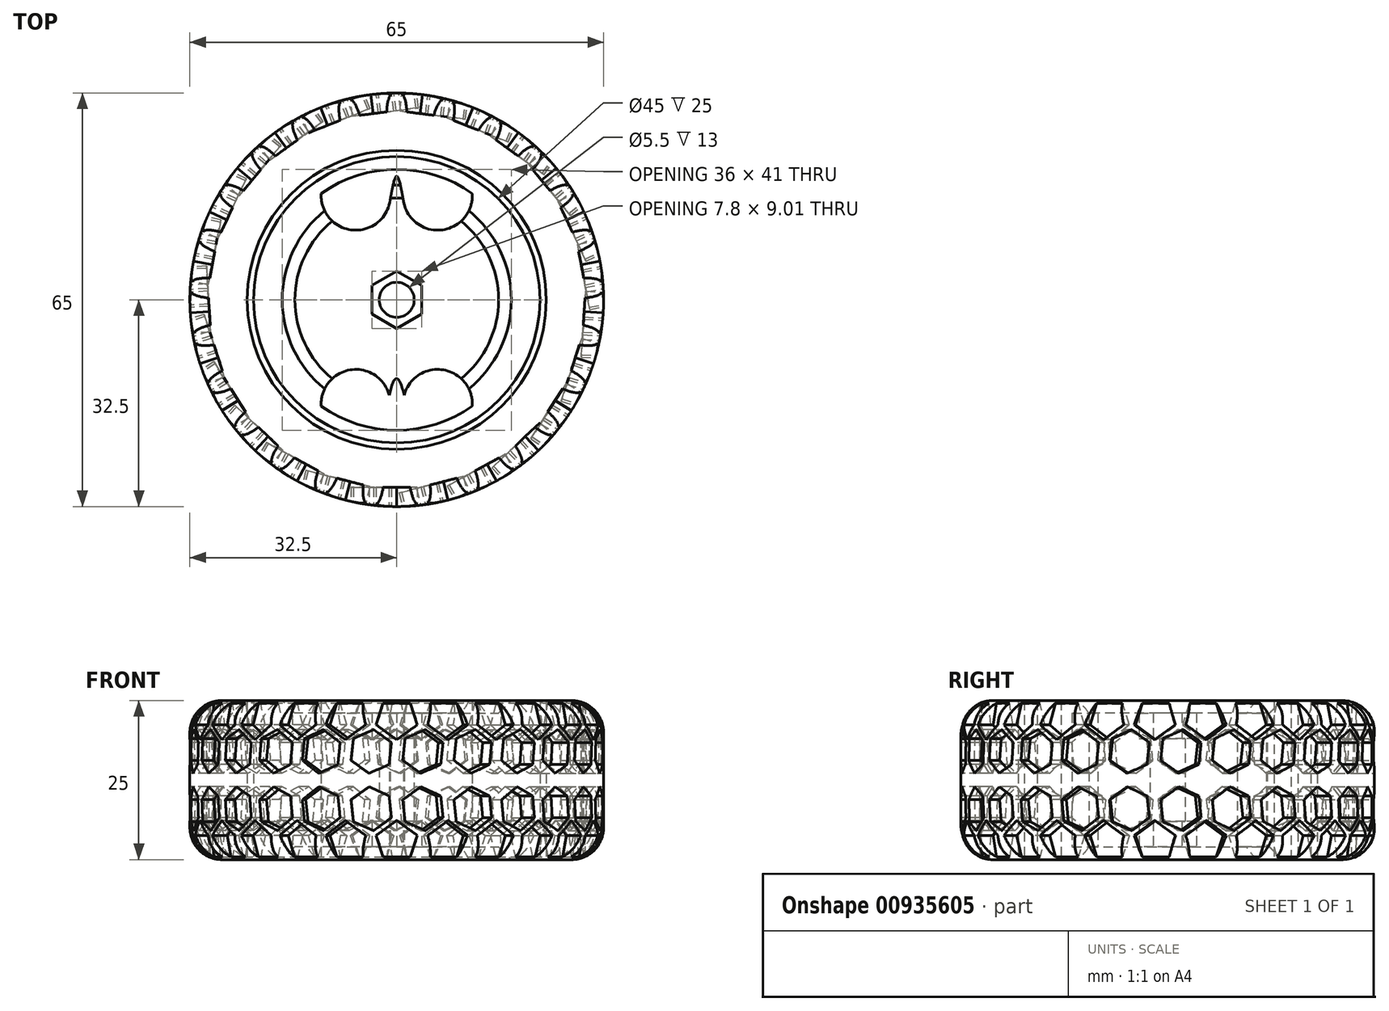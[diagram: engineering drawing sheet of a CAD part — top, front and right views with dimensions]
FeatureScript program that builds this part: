
annotation { "Feature Type Name" : "Feature", "Feature Type Description" : "" }
export const myFeature = defineFeature(function(context is Context, id is Id, definition is map)
    precondition{}
    {
        {
            var Q0;
            Q0=qCreatedBy(makeId("Top.planeOp"),FACE);
            var sketch = newSketch(context, id + "F0", { "sketchPlane" : qUnion([Q0])});
            skCircle(sketch, "E0", {"center": v(0, 0) * mm, "radius": 32.5 * mm});
            skCircle(sketch, "E1", {"center": v(0, 0) * mm, "radius": 22.5 * mm});
            skCircle(sketch, "E2", {"center": v(0, 0) * mm, "radius": 23.5 * mm});
            skCircle(sketch, "E3", {"center": v(0, 0) * mm, "radius": 20.5 * mm});
            skCircle(sketch, "E4", {"center": v(0, 0) * mm, "radius": 6 * mm});
            skCircle(sketch, "E5.cCircle", {"center": v(0, 0) * mm, "radius": 3.9 * mm, "construction": true});
            skLineSegment(sketch, "E5.0", {"start": v(-3.9, -2.25) * mm, "end": v(-3.9, 2.25) * mm});
            skLineSegment(sketch, "E5.1", {"start": v(-3.9, 2.25) * mm, "end": v(0, 4.5) * mm});
            skLineSegment(sketch, "E5.2", {"start": v(0, 4.5) * mm, "end": v(3.9, 2.25) * mm});
            skLineSegment(sketch, "E5.3", {"start": v(3.9, 2.25) * mm, "end": v(3.9, -2.25) * mm});
            skLineSegment(sketch, "E5.4", {"start": v(3.9, -2.25) * mm, "end": v(0, -4.5) * mm});
            skLineSegment(sketch, "E5.5", {"start": v(0, -4.5) * mm, "end": v(-3.9, -2.25) * mm});
            skPoint(sketch, "E5.0.midPoint", {"position": v(-3.9, 0) * mm});
            skCircle(sketch, "E6", {"center": v(0, 0) * mm, "radius": 3 * mm});
            skCircle(sketch, "E7", {"center": v(0, 0) * mm, "radius": 2.75 * mm});
            skArc(sketch, "E8", {"start": v(2.68, 20.32) * mm, "mid": v(4.44, 11.32) * mm, "end": v(11.87, 16.72) * mm});
            skArc(sketch, "E9.MirrorCS", {"start": v(-2.68, 20.32) * mm, "mid": v(-4.44, 11.32) * mm, "end": v(-11.87, 16.72) * mm});
            skArc(sketch, "E10.MirrorCS", {"start": v(-2.68, -20.32) * mm, "mid": v(-4.44, -11.32) * mm, "end": v(-11.87, -16.72) * mm});
            skArc(sketch, "E11.MirrorCS", {"start": v(2.68, -20.32) * mm, "mid": v(4.44, -11.32) * mm, "end": v(11.87, -16.72) * mm});
            skFitSpline(sketch, "E12", {"points": [v(-1.04, 15.65) * mm, v(0, 19.44) * mm, v(1.06, 15.51) * mm], "startDerivative": vector(2.1, 11.48) * mm, "endDerivative": vector(2.1, -11.69) * mm});
            skFitSpline(sketch, "E13", {"points": [v(-1.17, -15) * mm, v(1.17, -15) * mm], "startDerivative": vector(2.28, 10.68) * mm, "endDerivative": vector(2.46, -10.47) * mm});
            skSolve(sketch);
        }
        {
            var Q0;
            {var subQ0=sQuery(id+"F0.wireOp",EDGE,"820db2d4-8ff4-4f6f-a6e0-25a010e94ee20.MirrorCS");var subQ1=sQuery(id+"F0.wireOp",EDGE,"E3");var subQ2=makeQuery(id+"F0.imprint","INTERSECT",VERTEX,{"disambiguationData":[OD(0.0)],"derivedFrom":[subQ1,subQ0]});Q0=makeQuery(id+"F0.imprint","IMPRINT",FACE,{"disambiguationData":[TD([[makeQuery(id+"F0.imprint","IMPRINT",EDGE,{"disambiguationData":[TD([[subQ2,1.0]])],"derivedFrom":subQ1}),1.0]])]});}
            var Q1;
            Q1=makeQuery(id+"F0.imprint","IMPRINT",FACE,{"disambiguationData":[TD([[makeQuery(id+"F0.imprint","IMPRINT",EDGE,{"derivedFrom":sQuery(id+"F0.wireOp",EDGE,"E1")}),1.0]])]});
            var Q2;
            {var subQ0=sQuery(id+"F0.wireOp",EDGE,"fe73a623-ffbc-4a68-a9c5-13096b3fdf640.MirrorCS");var subQ1=sQuery(id+"F0.wireOp",EDGE,"E3");var subQ2=makeQuery(id+"F0.imprint","INTERSECT",VERTEX,{"disambiguationData":[OD(1.0)],"derivedFrom":[subQ1,subQ0]});Q2=makeQuery(id+"F0.imprint","IMPRINT",FACE,{"disambiguationData":[TD([[makeQuery(id+"F0.imprint","IMPRINT",EDGE,{"disambiguationData":[TD([[subQ2,1.0]])],"derivedFrom":subQ1}),1.0]])]});}
            var Q3;
            {var subQ0=sQuery(id+"F0.wireOp",EDGE,"6e8611d1-8290-4c50-aa15-6a44690360f50.MirrorCS");var subQ1=sQuery(id+"F0.wireOp",EDGE,"E3");var subQ2=makeQuery(id+"F0.imprint","INTERSECT",VERTEX,{"disambiguationData":[OD(1.0)],"derivedFrom":[subQ1,subQ0]});Q3=makeQuery(id+"F0.imprint","IMPRINT",FACE,{"disambiguationData":[TD([[makeQuery(id+"F0.imprint","IMPRINT",EDGE,{"disambiguationData":[TD([[subQ2,-1.0]])],"derivedFrom":subQ1}),1.0]])]});}
            var Q4;
            {var subQ0=sQuery(id+"F0.wireOp",EDGE,"6e8611d1-8290-4c50-aa15-6a44690360f50.MirrorCS");var subQ1=sQuery(id+"F0.wireOp",EDGE,"E3");var subQ2=makeQuery(id+"F0.imprint","INTERSECT",VERTEX,{"disambiguationData":[OD(0.0)],"derivedFrom":[subQ1,subQ0]});Q4=makeQuery(id+"F0.imprint","IMPRINT",FACE,{"disambiguationData":[TD([[makeQuery(id+"F0.imprint","IMPRINT",EDGE,{"disambiguationData":[TD([[subQ2,1.0]])],"derivedFrom":subQ1}),1.0]])]});}
            var Q5;
            Q5=makeQuery(id+"F0.imprint","IMPRINT",FACE,{"disambiguationData":[TD([[makeQuery(id+"F0.imprint","IMPRINT",EDGE,{"derivedFrom":sQuery(id+"F0.wireOp",EDGE,"E5.0")}),1.0]])]});
            var Q6;
            Q6=makeQuery(id+"F0.imprint","IMPRINT",FACE,{"disambiguationData":[TD([[makeQuery(id+"F0.imprint","IMPRINT",EDGE,{"derivedFrom":sQuery(id+"F0.wireOp",EDGE,"E5.0")}),-1.0]])]});
            var Q7;
            Q7=makeQuery(id+"F0.imprint","IMPRINT",FACE,{"disambiguationData":[TD([[makeQuery(id+"F0.imprint","IMPRINT",EDGE,{"derivedFrom":sQuery(id+"F0.wireOp",EDGE,"E1")}),-1.0]])]});
            var Q8;
            Q8=makeQuery(id+"F0.imprint","IMPRINT",FACE,{"disambiguationData":[TD([[makeQuery(id+"F0.imprint","IMPRINT",EDGE,{"derivedFrom":sQuery(id+"F0.wireOp",EDGE,"E4")}),-1.0]])]});
            extrude(context, id + "F1", {"entities" : qUnion([Q0, Q1, Q2, Q3, Q4, Q5, Q6, Q7, Q8]), "depth" : 25 * mm, "offsetDistance" : 25 * mm});
        }
        {
            var Q0;
            Q0=makeQuery(id+"F0.imprint","IMPRINT",FACE,{"disambiguationData":[TD([[makeQuery(id+"F0.imprint","IMPRINT",EDGE,{"derivedFrom":sQuery(id+"F0.wireOp",EDGE,"E0")}),1.0]])]});
            var Q1;
            Q1=makeQuery(id+"F0.imprint","IMPRINT",FACE,{"disambiguationData":[TD([[makeQuery(id+"F0.imprint","IMPRINT",EDGE,{"derivedFrom":sQuery(id+"F0.wireOp",EDGE,"E1")}),-1.0]])]});
            extrude(context, id + "F2", {"entities" : qUnion([Q0, Q1]), "depth" : 25 * mm, "offsetDistance" : 25 * mm});
        }
        {
            var Q0;
            Q0=makeQuery(id+"F0.imprint","IMPRINT",FACE,{"disambiguationData":[TD([[makeQuery(id+"F0.imprint","IMPRINT",EDGE,{"derivedFrom":sQuery(id+"F0.wireOp",EDGE,"E6")}),1.0]])]});
            extrude(context, id + "F3", {"entities" : qUnion([Q0]), "operationType" : NewBodyOperationType.ADD, "depth" : 23 * mm, "offsetDistance" : 25 * mm, "hasSecondDirection" : true, "secondDirectionOppositeDirection" : false, "secondDirectionDepth" : 2 * mm});
        }
        {
            var Q0;
            Q0=makeQuery(id+"F1.opExtrude","CAP_EDGE",EDGE,{"disambiguationData":[OSD([sQuery(id+"F0.wireOp",EDGE,"E6")])],"isStart":true});
            var Q1;
            Q1=makeQuery(id+"F1.opExtrude","CAP_EDGE",EDGE,{"disambiguationData":[OSD([sQuery(id+"F0.wireOp",EDGE,"E6")])],"isStart":false});
            chamfer(context, id + "F4", {"entities" : qUnion([Q0, Q1]), "width" : 15 * mm, "tangentPropagation" : true});
        }
        {
            var Q0;
            Q0=qCreatedBy(makeId("Front.planeOp"),FACE);
            cPlane(context, id + "F5", {"entities" : qUnion([Q0]), "cplaneType" : CPlaneType.OFFSET, "offset" : 32.5 * mm, "width" : 150 * mm, "height" : 150 * mm});
        }
        {
            var Q0;
            Q0=qCreatedBy(id+"F5.planeOp",FACE);
            var sketch = newSketch(context, id + "F6", { "sketchPlane" : qUnion([Q0])});
            skCircle(sketch, "E14.cCircle", {"center": v(0, 22.25) * mm, "radius": 2.75 * mm, "construction": true});
            skLineSegment(sketch, "E14.0", {"start": v(-2, 25) * mm, "end": v(2, 25) * mm});
            skLineSegment(sketch, "E14.1", {"start": v(2, 25) * mm, "end": v(3.24, 21.2) * mm});
            skLineSegment(sketch, "E14.2", {"start": v(3.24, 21.2) * mm, "end": v(0, 18.84) * mm});
            skLineSegment(sketch, "E14.3", {"start": v(0, 18.84) * mm, "end": v(-3.24, 21.2) * mm});
            skLineSegment(sketch, "E14.4", {"start": v(-3.24, 21.2) * mm, "end": v(-2, 25) * mm});
            skPoint(sketch, "E14.0.midPoint", {"position": v(0, 25) * mm});
            skLineSegment(sketch, "E15", {"start": v(-43.39, 12.5) * mm, "end": v(42.95, 12.5) * mm, "construction": true});
            skCircle(sketch, "E16.cCircle", {"center": v(-4, 17) * mm, "radius": 3 * mm, "construction": true});
            skLineSegment(sketch, "E16.0", {"start": v(-3.64, 20.45) * mm, "end": v(-0.84, 18.4) * mm});
            skLineSegment(sketch, "E16.1", {"start": v(-0.84, 18.4) * mm, "end": v(-1.2, 14.96) * mm});
            skLineSegment(sketch, "E16.2", {"start": v(-1.2, 14.96) * mm, "end": v(-4.36, 13.55) * mm});
            skLineSegment(sketch, "E16.3", {"start": v(-4.36, 13.55) * mm, "end": v(-7.16, 15.6) * mm});
            skLineSegment(sketch, "E16.4", {"start": v(-7.16, 15.6) * mm, "end": v(-6.8, 19.04) * mm});
            skLineSegment(sketch, "E16.5", {"start": v(-6.8, 19.04) * mm, "end": v(-3.64, 20.45) * mm});
            skPoint(sketch, "E16.0.midPoint", {"position": v(-2.24, 19.43) * mm});
            skLineSegment(sketch, "E17.MirrorCS", {"start": v(-6.8, 5.96) * mm, "end": v(-3.64, 4.55) * mm});
            skCircle(sketch, "E18.MirrorC", {"center": v(-4, 8) * mm, "radius": 3 * mm, "construction": true});
            skLineSegment(sketch, "E19.MirrorCS", {"start": v(-3.64, 4.55) * mm, "end": v(-0.84, 6.6) * mm});
            skLineSegment(sketch, "E20.MirrorCS", {"start": v(-0.84, 6.6) * mm, "end": v(-1.2, 10.04) * mm});
            skLineSegment(sketch, "E21.MirrorCS", {"start": v(-1.2, 10.04) * mm, "end": v(-4.36, 11.45) * mm});
            skLineSegment(sketch, "E22.MirrorCS", {"start": v(-4.36, 11.45) * mm, "end": v(-7.16, 9.4) * mm});
            skLineSegment(sketch, "E23.MirrorCS", {"start": v(-7.16, 9.4) * mm, "end": v(-6.8, 5.96) * mm});
            skPoint(sketch, "E24.MirrorP", {"position": v(0, 0) * mm});
            skLineSegment(sketch, "E25.MirrorCS", {"start": v(-2, 0) * mm, "end": v(2, 0) * mm});
            skLineSegment(sketch, "E26.MirrorCS", {"start": v(-3.24, 3.8) * mm, "end": v(-2, 0) * mm});
            skLineSegment(sketch, "E27.MirrorCS", {"start": v(3.24, 3.8) * mm, "end": v(0, 6.16) * mm});
            skLineSegment(sketch, "E28.MirrorCS", {"start": v(0, 6.16) * mm, "end": v(-3.24, 3.8) * mm});
            skPoint(sketch, "E29.MirrorP", {"position": v(-2.24, 5.57) * mm});
            skCircle(sketch, "E30.MirrorC", {"center": v(0, 2.75) * mm, "radius": 2.75 * mm, "construction": true});
            skLineSegment(sketch, "E31.MirrorCS", {"start": v(2, 0) * mm, "end": v(3.24, 3.8) * mm});
            skSolve(sketch);
        }
        {
            var Q0;
            Q0=makeQuery(id+"F6.imprint","IMPRINT",FACE,{"disambiguationData":[TD([[makeQuery(id+"F6.imprint","IMPRINT",EDGE,{"derivedFrom":sQuery(id+"F6.wireOp",EDGE,"E14.0")}),-1.0]])]});
            var Q1;
            Q1=makeQuery(id+"F6.imprint","IMPRINT",FACE,{"disambiguationData":[TD([[makeQuery(id+"F6.imprint","IMPRINT",EDGE,{"derivedFrom":sQuery(id+"F6.wireOp",EDGE,"E16.0")}),-1.0]])]});
            var Q2;
            Q2=makeQuery(id+"F6.imprint","IMPRINT",FACE,{"disambiguationData":[TD([[makeQuery(id+"F6.imprint","IMPRINT",EDGE,{"derivedFrom":sQuery(id+"F6.wireOp",EDGE,"E17.MirrorCS")}),1.0]])]});
            var Q3;
            Q3=makeQuery(id+"F6.imprint","IMPRINT",FACE,{"disambiguationData":[TD([[makeQuery(id+"F6.imprint","IMPRINT",EDGE,{"derivedFrom":sQuery(id+"F6.wireOp",EDGE,"E25.MirrorCS")}),1.0]])]});
            extrude(context, id + "F7", {"entities" : qUnion([Q0, Q1, Q2, Q3]), "oppositeDirection" : true, "depth" : 3 * mm, "offsetDistance" : 25 * mm});
        }
        {
            var Q0;
            Q0=makeQuery(id+"F2.opExtrude","CAP_EDGE",EDGE,{"disambiguationData":[OSD([sQuery(id+"F0.wireOp",EDGE,"E0")])],"isStart":false});
            var Q1;
            Q1=makeQuery(id+"F2.opExtrude","CAP_EDGE",EDGE,{"disambiguationData":[OSD([sQuery(id+"F0.wireOp",EDGE,"E0")])],"isStart":true});
            fillet(context, id + "F8", {"entities" : qUnion([Q0, Q1]), "radius" : 5 * mm, "tangentPropagation" : true, "allowEdgeOverflow" : false});
        }
        {
            var Q0;
            Q0=makeQuery(id+"F7.opExtrude","SWEPT_BODY",BODY,{"disambiguationData":[OSD([sQuery(id+"F6.wireOp",EDGE,"E14.0"),sQuery(id+"F6.wireOp",EDGE,"E14.1"),sQuery(id+"F6.wireOp",EDGE,"E14.2"),sQuery(id+"F6.wireOp",EDGE,"E14.3"),sQuery(id+"F6.wireOp",EDGE,"E14.4")])]});
            var Q1;
            Q1=makeQuery(id+"F7.opExtrude","SWEPT_BODY",BODY,{"disambiguationData":[OSD([sQuery(id+"F6.wireOp",EDGE,"E16.0"),sQuery(id+"F6.wireOp",EDGE,"E16.1"),sQuery(id+"F6.wireOp",EDGE,"E16.2"),sQuery(id+"F6.wireOp",EDGE,"E16.3"),sQuery(id+"F6.wireOp",EDGE,"E16.4"),sQuery(id+"F6.wireOp",EDGE,"E16.5")])]});
            var Q2;
            Q2=makeQuery(id+"F7.opExtrude","SWEPT_BODY",BODY,{"disambiguationData":[OSD([sQuery(id+"F6.wireOp",EDGE,"E17.MirrorCS"),sQuery(id+"F6.wireOp",EDGE,"E20.MirrorCS"),sQuery(id+"F6.wireOp",EDGE,"E21.MirrorCS"),sQuery(id+"F6.wireOp",EDGE,"E22.MirrorCS"),sQuery(id+"F6.wireOp",EDGE,"E23.MirrorCS"),sQuery(id+"F6.wireOp",EDGE,"E19.MirrorCS")])]});
            var Q3;
            Q3=makeQuery(id+"F7.opExtrude","SWEPT_BODY",BODY,{"disambiguationData":[OSD([sQuery(id+"F6.wireOp",EDGE,"E25.MirrorCS"),sQuery(id+"F6.wireOp",EDGE,"E26.MirrorCS"),sQuery(id+"F6.wireOp",EDGE,"E28.MirrorCS"),sQuery(id+"F6.wireOp",EDGE,"E27.MirrorCS"),sQuery(id+"F6.wireOp",EDGE,"E31.MirrorCS")])]});
            var Q4;
            {var subQ0=sQuery(id+"F0.wireOp",EDGE,"E0");Q4=makeQuery(id+"F8.opFillet","BLEND_FACE",FACE,{"disambiguationData":[OSD([subQ0]),TDD([makeQuery(id+"F2.opExtrude","CAP_EDGE",EDGE,{"disambiguationData":[OSD([subQ0])],"isStart":false})])]});}
            circularPattern(context, id + "F9", {"operationType" : NewBodyOperationType.REMOVE, "entities" : qUnion([Q0, Q1, Q2, Q3]), "axis" : qUnion([Q4]), "angle" : 360 * degree, "instanceCount" : 25, "equalSpace" : true});
        }
        {
            var Q0;
            Q0=makeQuery(id+"F0.imprint","IMPRINT",FACE,{"disambiguationData":[TD([[makeQuery(id+"F0.imprint","IMPRINT",EDGE,{"derivedFrom":sQuery(id+"F0.wireOp",EDGE,"E5.0")}),-1.0]])]});
            var Q1;
            Q1=makeQuery(id+"F0.imprint","IMPRINT",FACE,{"disambiguationData":[TD([[makeQuery(id+"F0.imprint","IMPRINT",EDGE,{"derivedFrom":sQuery(id+"F0.wireOp",EDGE,"E6")}),1.0]])]});
            extrude(context, id + "F10", {"entities" : qUnion([Q0, Q1]), "operationType" : NewBodyOperationType.REMOVE, "depth" : 6 * mm, "offsetDistance" : 25 * mm});
        }
        {
            var Q0;
            Q0=makeQuery(id+"F0.imprint","IMPRINT",FACE,{"disambiguationData":[TD([[makeQuery(id+"F0.imprint","IMPRINT",EDGE,{"derivedFrom":sQuery(id+"F0.wireOp",EDGE,"E5.0")}),-1.0]])]});
            var Q1;
            Q1=makeQuery(id+"F0.imprint","IMPRINT",FACE,{"disambiguationData":[TD([[makeQuery(id+"F0.imprint","IMPRINT",EDGE,{"derivedFrom":sQuery(id+"F0.wireOp",EDGE,"E6")}),1.0]])]});
            extrude(context, id + "F11", {"entities" : qUnion([Q0, Q1]), "operationType" : NewBodyOperationType.REMOVE, "depth" : 25 * mm, "offsetDistance" : 25 * mm, "hasSecondDirection" : true, "secondDirectionOppositeDirection" : false, "secondDirectionDepth" : 19 * mm});
        }
    });
